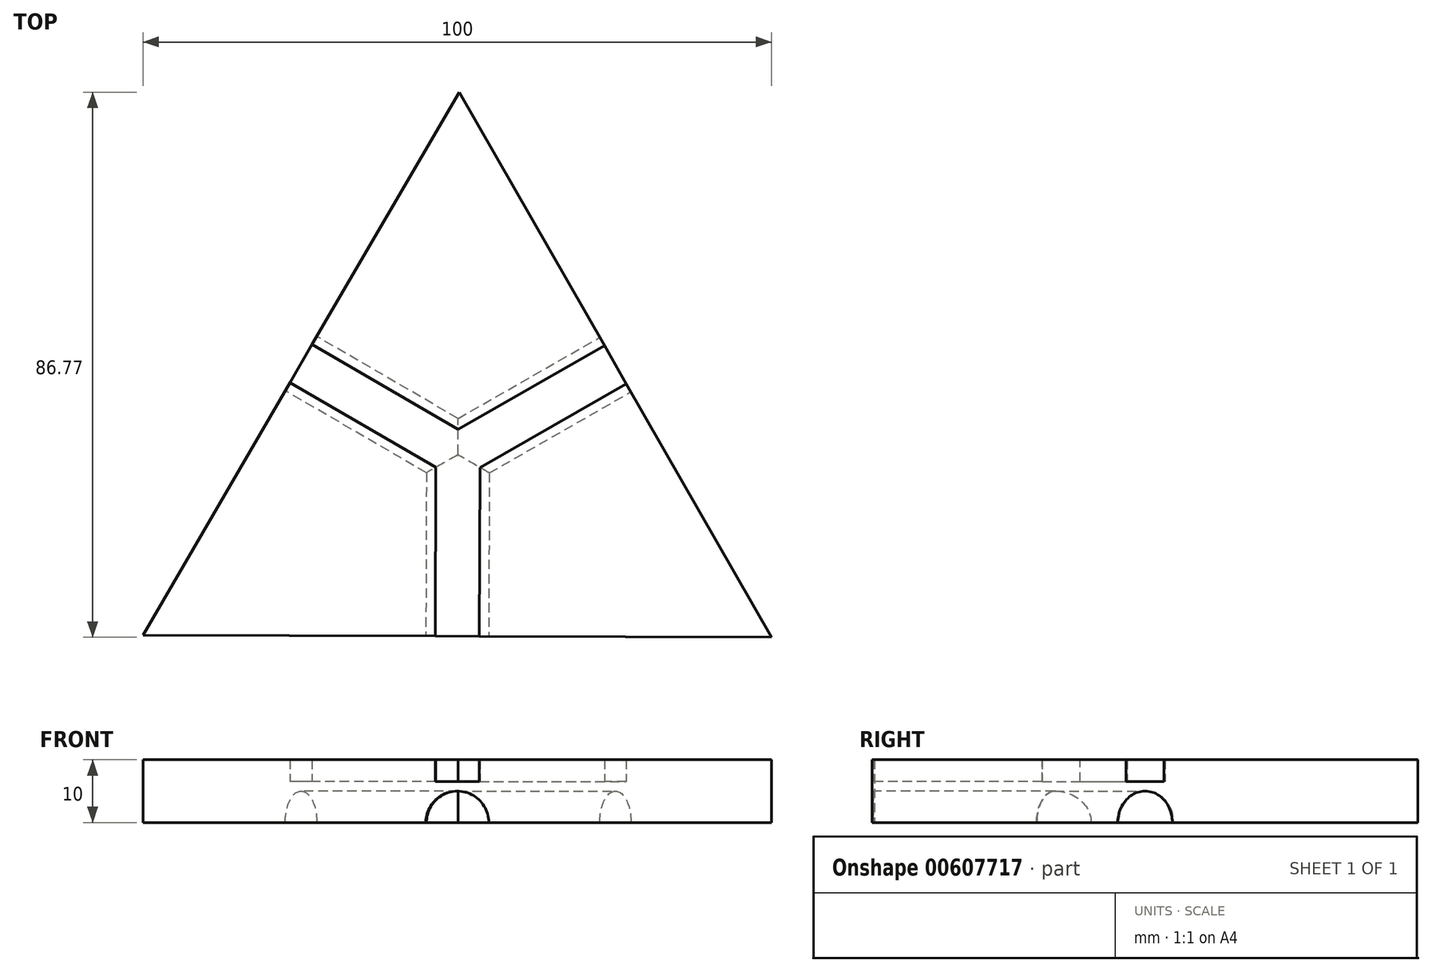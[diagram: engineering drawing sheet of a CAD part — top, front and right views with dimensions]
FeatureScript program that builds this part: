
annotation { "Feature Type Name" : "Feature", "Feature Type Description" : "" }
export const myFeature = defineFeature(function(context is Context, id is Id, definition is map)
    precondition{}
    {
        {
            var Q0;
            Q0=qCreatedBy(makeId("Top.planeOp"),FACE);
            var sketch = newSketch(context, id + "F0", { "sketchPlane" : qUnion([Q0])});
            skCircle(sketch, "E0.cCircle", {"center": v(0, 0) * mm, "radius": 28.87 * mm, "construction": true});
            skLineSegment(sketch, "E0.0", {"start": v(0.2, 57.73) * mm, "end": v(49.9, -29.04) * mm});
            skLineSegment(sketch, "E0.1", {"start": v(49.9, -29.04) * mm, "end": v(-50.1, -28.7) * mm});
            skLineSegment(sketch, "E0.2", {"start": v(-50.1, -28.7) * mm, "end": v(0.2, 57.73) * mm});
            skPoint(sketch, "E0.0.midPoint", {"position": v(25.05, 14.35) * mm});
            skSolve(sketch);
        }
        {
            var Q0;
            Q0=makeQuery(id+"F0.imprint","IMPRINT",FACE,{"disambiguationData":[TD([[makeQuery(id+"F0.imprint","IMPRINT",EDGE,{"derivedFrom":sQuery(id+"F0.wireOp",EDGE,"E0.0")}),-1.0]])]});
            extrude(context, id + "F1", {"entities" : qUnion([Q0]), "depth" : 10 * mm, "offsetDistance" : 25 * mm});
        }
        {
            var Q0;
            Q0=makeQuery(id+"F1.opExtrude","SWEPT_FACE",FACE,{"disambiguationData":[OSD([sQuery(id+"F0.wireOp",EDGE,"E0.1")])]});
            var sketch = newSketch(context, id + "F2", { "sketchPlane" : qUnion([Q0])});
            skCircle(sketch, "E1", {"center": v(0, 0) * mm, "radius": 5 * mm});
            skSolve(sketch);
        }
        {
            var Q0;
            {var subQ0=sQuery(id+"F2.wireOp",EDGE,"E1");var subQ1=makeQuery(id+"F1.opExtrude","CAP_EDGE",EDGE,{"disambiguationData":[OSD([sQuery(id+"F0.wireOp",EDGE,"E0.1")])],"isStart":true});var subQ2=makeQuery(id+"F2.imprint","INTERSECT",VERTEX,{"disambiguationData":[OD(0.0)],"derivedFrom":[subQ1,subQ0]});Q0=makeQuery(id+"F2.imprint","IMPRINT",FACE,{"disambiguationData":[TD([[makeQuery(id+"F2.imprint","IMPRINT",EDGE,{"disambiguationData":[TD([[subQ2,-1.0]])],"derivedFrom":subQ0}),1.0]])]});}
            extrude(context, id + "F3", {"entities" : qUnion([Q0]), "operationType" : NewBodyOperationType.REMOVE, "oppositeDirection" : true, "depth" : 29 * mm, "offsetDistance" : 25 * mm});
        }
        {
            var Q0;
            Q0=makeQuery(id+"F1.opExtrude","SWEPT_FACE",FACE,{"disambiguationData":[OSD([sQuery(id+"F0.wireOp",EDGE,"E0.2")])]});
            var sketch = newSketch(context, id + "F4", { "sketchPlane" : qUnion([Q0])});
            skCircle(sketch, "E2", {"center": v(0, 0) * mm, "radius": 5 * mm});
            skSolve(sketch);
        }
        {
            var Q0;
            {var subQ0=sQuery(id+"F4.wireOp",EDGE,"E2");var subQ1=makeQuery(id+"F1.opExtrude","CAP_EDGE",EDGE,{"disambiguationData":[OSD([sQuery(id+"F0.wireOp",EDGE,"E0.2")])],"isStart":true});var subQ2=makeQuery(id+"F4.imprint","INTERSECT",VERTEX,{"disambiguationData":[OD(0.0)],"derivedFrom":[subQ1,subQ0]});Q0=makeQuery(id+"F4.imprint","IMPRINT",FACE,{"disambiguationData":[TD([[makeQuery(id+"F4.imprint","IMPRINT",EDGE,{"disambiguationData":[TD([[subQ2,1.0]])],"derivedFrom":subQ0}),1.0]])]});}
            var Q1;
            Q1=sQuery(id+"F4.wireOp",EDGE,"E2");
            extrude(context, id + "F5", {"entities" : qUnion([Q0]), "operationType" : NewBodyOperationType.REMOVE, "surfaceEntities" : qUnion([Q1]), "oppositeDirection" : true, "depth" : 29 * mm, "offsetDistance" : 25 * mm});
        }
        {
            var Q0;
            Q0=makeQuery(id+"F1.opExtrude","SWEPT_FACE",FACE,{"disambiguationData":[OSD([sQuery(id+"F0.wireOp",EDGE,"E0.0")])]});
            var sketch = newSketch(context, id + "F6", { "sketchPlane" : qUnion([Q0])});
            skCircle(sketch, "E3", {"center": v(0, 0) * mm, "radius": 5 * mm});
            skSolve(sketch);
        }
        {
            var Q0;
            {var subQ0=sQuery(id+"F6.wireOp",EDGE,"E3");var subQ1=makeQuery(id+"F1.opExtrude","CAP_EDGE",EDGE,{"disambiguationData":[OSD([sQuery(id+"F0.wireOp",EDGE,"E0.0")])],"isStart":true});var subQ2=makeQuery(id+"F6.imprint","INTERSECT",VERTEX,{"disambiguationData":[OD(0.0)],"derivedFrom":[subQ1,subQ0]});Q0=makeQuery(id+"F6.imprint","IMPRINT",FACE,{"disambiguationData":[TD([[makeQuery(id+"F6.imprint","IMPRINT",EDGE,{"disambiguationData":[TD([[subQ2,-1.0]])],"derivedFrom":subQ0}),1.0]])]});}
            extrude(context, id + "F7", {"entities" : qUnion([Q0]), "operationType" : NewBodyOperationType.REMOVE, "oppositeDirection" : true, "depth" : 29 * mm, "offsetDistance" : 25 * mm});
        }
        {
            var Q0;
            Q0=makeQuery(id+"F1.opExtrude","SWEPT_FACE",FACE,{"disambiguationData":[OSD([sQuery(id+"F0.wireOp",EDGE,"E0.0")])]});
            var sketch = newSketch(context, id + "F8", { "sketchPlane" : qUnion([Q0])});
            skLineSegment(sketch, "E4.bottom", {"start": v(-3.5, 13.5) * mm, "end": v(3.5, 13.5) * mm});
            skLineSegment(sketch, "E4.top", {"start": v(-3.5, 6.5) * mm, "end": v(3.5, 6.5) * mm});
            skLineSegment(sketch, "E4.left", {"start": v(-3.5, 13.5) * mm, "end": v(-3.5, 6.5) * mm});
            skLineSegment(sketch, "E4.right", {"start": v(3.5, 13.5) * mm, "end": v(3.5, 6.5) * mm});
            skPoint(sketch, "E4.middle", {"position": v(0, 10) * mm});
            skSolve(sketch);
        }
        {
            var Q0;
            {var subQ0=sQuery(id+"F8.wireOp",EDGE,"E4.top");Q0=makeQuery(id+"F8.imprint","IMPRINT",FACE,{"disambiguationData":[TD([[makeQuery(id+"F8.imprint","IMPRINT",EDGE,{"derivedFrom":subQ0}),1.0]])]});}
            extrude(context, id + "F9", {"entities" : qUnion([Q0]), "operationType" : NewBodyOperationType.REMOVE, "oppositeDirection" : true, "depth" : 29 * mm, "offsetDistance" : 25 * mm});
        }
        {
            var Q0;
            Q0=makeQuery(id+"F1.opExtrude","SWEPT_FACE",FACE,{"disambiguationData":[OSD([sQuery(id+"F0.wireOp",EDGE,"E0.2")])]});
            var sketch = newSketch(context, id + "F10", { "sketchPlane" : qUnion([Q0])});
            skLineSegment(sketch, "E5.bottom", {"start": v(-3.5, 13.5) * mm, "end": v(3.5, 13.5) * mm});
            skLineSegment(sketch, "E5.top", {"start": v(-3.5, 6.5) * mm, "end": v(3.5, 6.5) * mm});
            skLineSegment(sketch, "E5.left", {"start": v(-3.5, 13.5) * mm, "end": v(-3.5, 6.5) * mm});
            skLineSegment(sketch, "E5.right", {"start": v(3.5, 13.5) * mm, "end": v(3.5, 6.5) * mm});
            skPoint(sketch, "E5.middle", {"position": v(0, 10) * mm});
            skSolve(sketch);
        }
        {
            var Q0;
            {var subQ0=sQuery(id+"F10.wireOp",EDGE,"E5.top");Q0=makeQuery(id+"F10.imprint","IMPRINT",FACE,{"disambiguationData":[TD([[makeQuery(id+"F10.imprint","IMPRINT",EDGE,{"derivedFrom":subQ0}),1.0]])]});}
            extrude(context, id + "F11", {"entities" : qUnion([Q0]), "operationType" : NewBodyOperationType.REMOVE, "oppositeDirection" : true, "depth" : 29 * mm, "offsetDistance" : 25 * mm});
        }
        {
            var Q0;
            Q0=makeQuery(id+"F1.opExtrude","SWEPT_FACE",FACE,{"disambiguationData":[OSD([sQuery(id+"F0.wireOp",EDGE,"E0.1")])]});
            var sketch = newSketch(context, id + "F12", { "sketchPlane" : qUnion([Q0])});
            skLineSegment(sketch, "E6.bottom", {"start": v(-3.5, 13.5) * mm, "end": v(3.5, 13.5) * mm});
            skLineSegment(sketch, "E6.top", {"start": v(-3.5, 6.5) * mm, "end": v(3.5, 6.5) * mm});
            skLineSegment(sketch, "E6.left", {"start": v(-3.5, 13.5) * mm, "end": v(-3.5, 6.5) * mm});
            skLineSegment(sketch, "E6.right", {"start": v(3.5, 13.5) * mm, "end": v(3.5, 6.5) * mm});
            skPoint(sketch, "E6.middle", {"position": v(0, 10) * mm});
            skSolve(sketch);
        }
        {
            var Q0;
            {var subQ0=sQuery(id+"F12.wireOp",EDGE,"E6.top");Q0=makeQuery(id+"F12.imprint","IMPRINT",FACE,{"disambiguationData":[TD([[makeQuery(id+"F12.imprint","IMPRINT",EDGE,{"derivedFrom":subQ0}),1.0]])]});}
            extrude(context, id + "F13", {"entities" : qUnion([Q0]), "operationType" : NewBodyOperationType.REMOVE, "oppositeDirection" : true, "depth" : 29 * mm, "offsetDistance" : 25 * mm});
        }
    });
